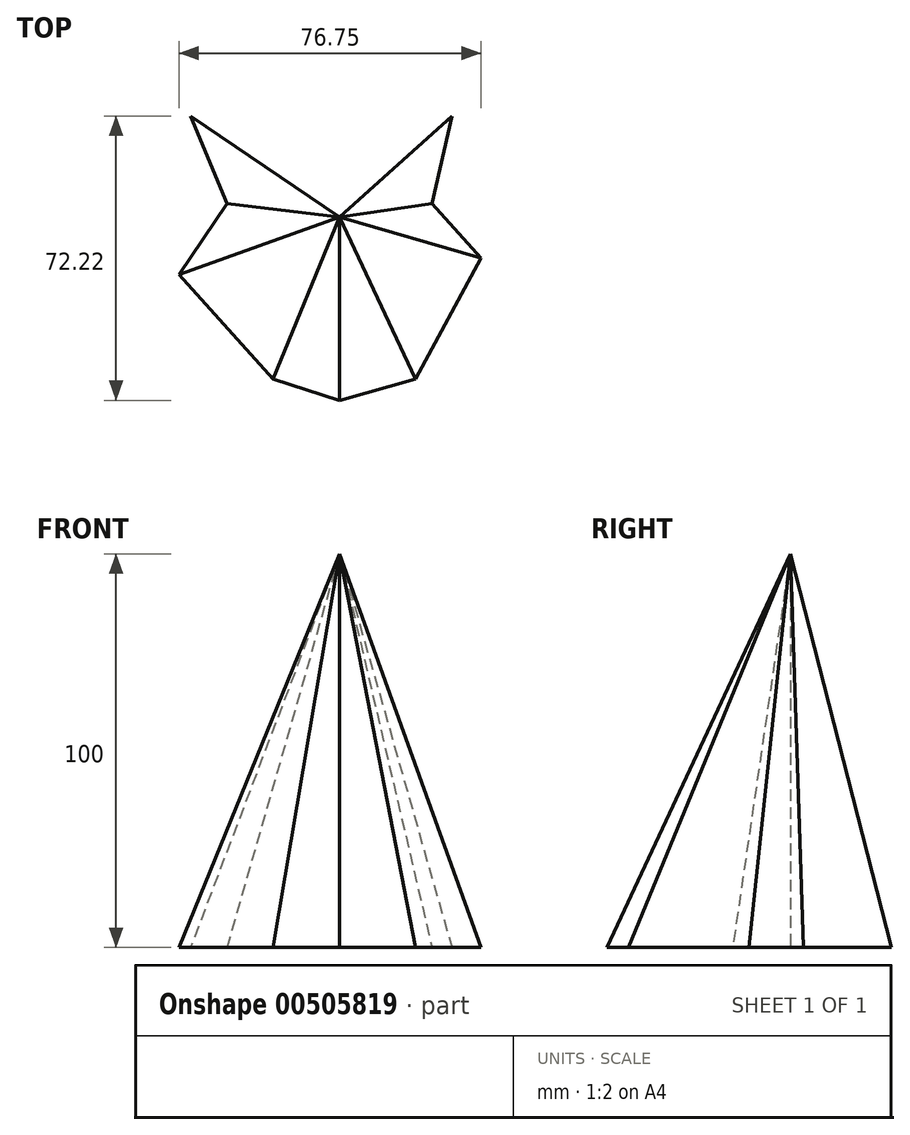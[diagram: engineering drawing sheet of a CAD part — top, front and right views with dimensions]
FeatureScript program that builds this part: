
annotation { "Feature Type Name" : "Feature", "Feature Type Description" : "" }
export const myFeature = defineFeature(function(context is Context, id is Id, definition is map)
    precondition{}
    {
        {
            var Q0;
            Q0=qCreatedBy(makeId("Top.planeOp"),FACE);
            var sketch = newSketch(context, id + "F0", { "sketchPlane" : qUnion([Q0])});
            skLineSegment(sketch, "E0", {"start": v(0, 0) * mm, "end": v(-37.87, 25.65) * mm});
            skLineSegment(sketch, "E1", {"start": v(0, 0) * mm, "end": v(28.47, 25.65) * mm});
            skLineSegment(sketch, "E2", {"start": v(28.47, 25.65) * mm, "end": v(23.43, 3.4) * mm});
            skLineSegment(sketch, "E3", {"start": v(-37.87, 25.65) * mm, "end": v(-28.63, 3.4) * mm});
            skLineSegment(sketch, "E4", {"start": v(-28.63, 3.4) * mm, "end": v(-40.84, -14.64) * mm});
            skLineSegment(sketch, "E5", {"start": v(23.43, 3.4) * mm, "end": v(35.9, -10.45) * mm});
            skLineSegment(sketch, "E6", {"start": v(35.9, -10.45) * mm, "end": v(19.24, -41.11) * mm});
            skLineSegment(sketch, "E7", {"start": v(-40.84, -14.64) * mm, "end": v(-17, -41.11) * mm});
            skLineSegment(sketch, "E8", {"start": v(-17, -41.11) * mm, "end": v(0, -46.57) * mm});
            skLineSegment(sketch, "E9", {"start": v(19.24, -41.11) * mm, "end": v(0, -46.57) * mm});
            skSolve(sketch);
        }
        {
            var Q0;
            Q0=qCreatedBy(makeId("Top.planeOp"),FACE);
            cPlane(context, id + "F1", {"entities" : qUnion([Q0]), "cplaneType" : CPlaneType.OFFSET, "offset" : 100 * mm, "width" : 150 * mm, "height" : 150 * mm});
        }
        {
            var Q0;
            Q0=qCreatedBy(id+"F1.planeOp",FACE);
            var sketch = newSketch(context, id + "F2", { "sketchPlane" : qUnion([Q0])});
            skPoint(sketch, "E10", {"position": v(0, 0) * mm});
            skSolve(sketch);
        }
        {
            var Q0;
            Q0=sQuery(id+"F2.wireOp",VERTEX,"E10");
            var Q1;
            Q1=makeQuery(id+"F0.imprint","IMPRINT",FACE,{"disambiguationData":[TD([[makeQuery(id+"F0.imprint","IMPRINT",EDGE,{"derivedFrom":sQuery(id+"F0.wireOp",EDGE,"E0")}),1.0]])]});
            loft(context, id + "F3", {"sheetProfilesArray" : [{ "sheetProfileEntities" : qUnion([Q0]) }, { "sheetProfileEntities" : qUnion([Q1]) }]});
        }
    });
